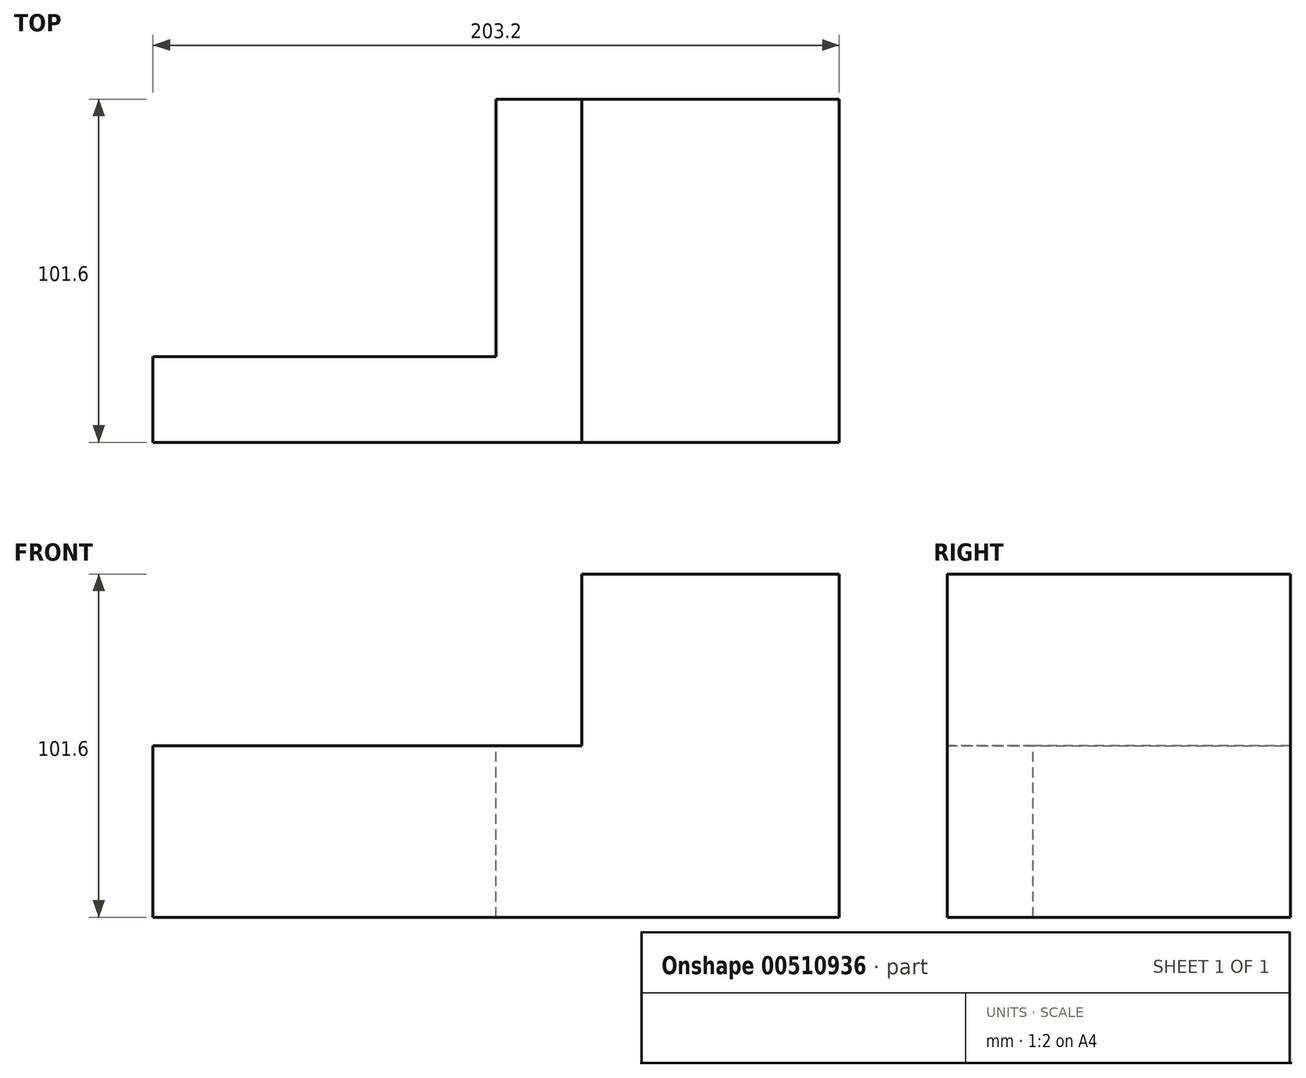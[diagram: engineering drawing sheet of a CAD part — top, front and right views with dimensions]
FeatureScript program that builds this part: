
annotation { "Feature Type Name" : "Feature", "Feature Type Description" : "" }
export const myFeature = defineFeature(function(context is Context, id is Id, definition is map)
    precondition{}
    {
        {
            var Q0;
            Q0=qCreatedBy(makeId("Top.planeOp"),FACE);
            var sketch = newSketch(context, id + "F0", { "sketchPlane" : qUnion([Q0])});
            skLineSegment(sketch, "E0.bottom", {"start": v(0, 0) * mm, "end": v(-203.2, 0) * mm});
            skLineSegment(sketch, "E0.top", {"start": v(0, -101.6) * mm, "end": v(-203.2, -101.6) * mm});
            skLineSegment(sketch, "E0.left", {"start": v(0, 0) * mm, "end": v(0, -101.6) * mm});
            skLineSegment(sketch, "E0.right", {"start": v(-203.2, 0) * mm, "end": v(-203.2, -101.6) * mm});
            skSolve(sketch);
        }
        {
            var Q0;
            Q0 = qSketchRegion(id + "F0", true);
            extrude(context, id + "F1", {"entities" : qUnion([Q0]), "depth" : 101.6 * mm});
        }
        {
            var Q0;
            Q0=makeQuery(id+"F1.opExtrude","CAP_FACE",FACE,{"disambiguationData":[OSD([sQuery(id+"F0.wireOp",EDGE,"E0.bottom"),sQuery(id+"F0.wireOp",EDGE,"E0.top"),sQuery(id+"F0.wireOp",EDGE,"E0.left"),sQuery(id+"F0.wireOp",EDGE,"E0.right")])],"isStart":false});
            var sketch = newSketch(context, id + "F2", { "sketchPlane" : qUnion([Q0])});
            skLineSegment(sketch, "E1.bottom", {"start": v(-203.2, -101.6) * mm, "end": v(-76.2, -101.6) * mm});
            skLineSegment(sketch, "E1.top", {"start": v(-203.2, 0) * mm, "end": v(-76.2, 0) * mm});
            skLineSegment(sketch, "E1.left", {"start": v(-203.2, -101.6) * mm, "end": v(-203.2, 0) * mm});
            skLineSegment(sketch, "E1.right", {"start": v(-76.2, -101.6) * mm, "end": v(-76.2, 0) * mm});
            skSolve(sketch);
        }
        {
            var Q0;
            Q0 = qSketchRegion(id + "F2", true);
            extrude(context, id + "F3", {"entities" : qUnion([Q0]), "operationType" : NewBodyOperationType.REMOVE, "oppositeDirection" : true, "depth" : 50.8 * mm});
        }
        {
            var Q0;
            Q0=makeQuery(id+"F3.boolean.opBoolean","COPY",FACE,{"derivedFrom":makeQuery(id+"F3.opExtrude","CAP_FACE",FACE,{"disambiguationData":[OSD([sQuery(id+"F2.wireOp",EDGE,"E1.bottom"),sQuery(id+"F2.wireOp",EDGE,"E1.top"),sQuery(id+"F2.wireOp",EDGE,"E1.left"),sQuery(id+"F2.wireOp",EDGE,"E1.right")])],"isStart":false})});
            var sketch = newSketch(context, id + "F4", { "sketchPlane" : qUnion([Q0])});
            skLineSegment(sketch, "E2.bottom", {"start": v(-203.2, 0) * mm, "end": v(-101.6, 0) * mm});
            skLineSegment(sketch, "E2.top", {"start": v(-203.2, -76.2) * mm, "end": v(-101.6, -76.2) * mm});
            skLineSegment(sketch, "E2.left", {"start": v(-203.2, 0) * mm, "end": v(-203.2, -76.2) * mm});
            skLineSegment(sketch, "E2.right", {"start": v(-101.6, 0) * mm, "end": v(-101.6, -76.2) * mm});
            skSolve(sketch);
        }
        {
            var Q0;
            Q0 = qSketchRegion(id + "F4", true);
            extrude(context, id + "F5", {"entities" : qUnion([Q0]), "operationType" : NewBodyOperationType.REMOVE, "oppositeDirection" : true, "depth" : 50.8 * mm});
        }
    });
